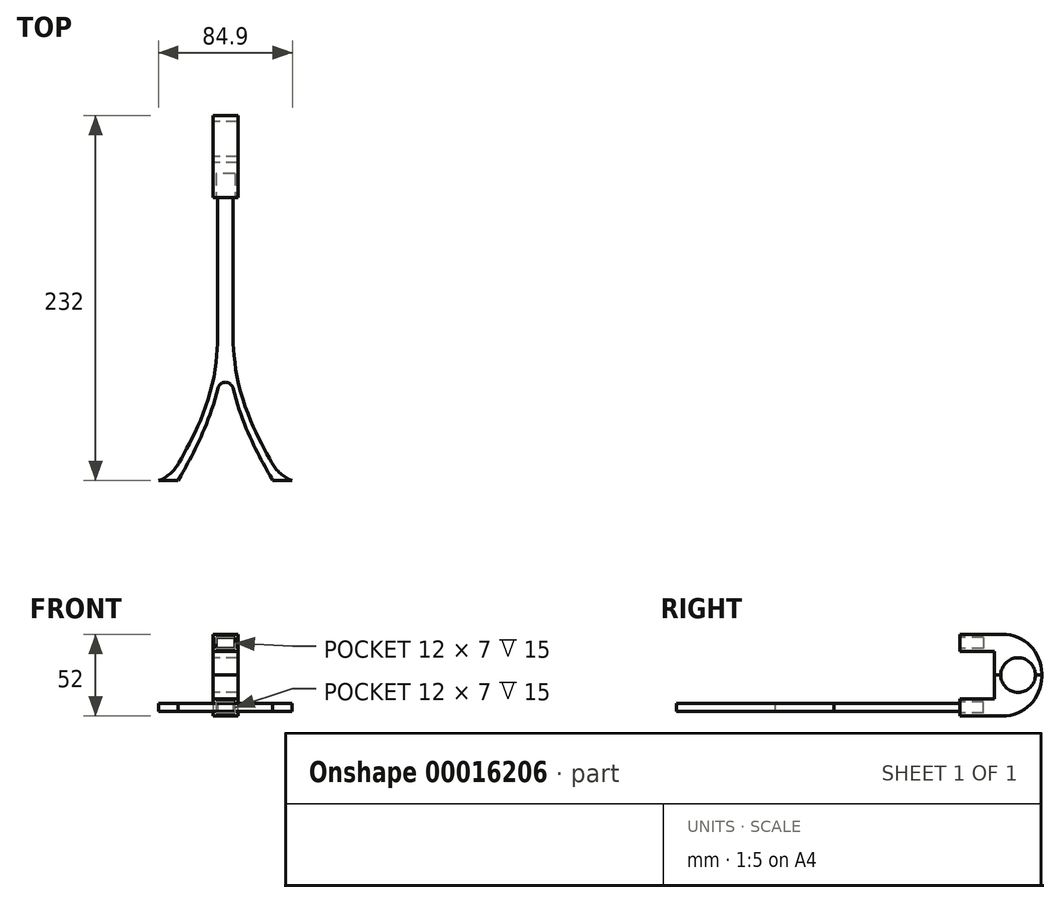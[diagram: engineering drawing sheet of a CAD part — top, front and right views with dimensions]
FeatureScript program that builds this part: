
annotation { "Feature Type Name" : "Feature", "Feature Type Description" : "" }
export const myFeature = defineFeature(function(context is Context, id is Id, definition is map)
    precondition{}
    {
        {
            var Q0;
            Q0=qCreatedBy(makeId("Top.planeOp"),FACE);
            var sketch = newSketch(context, id + "F0", { "sketchPlane" : qUnion([Q0])});
            skLineSegment(sketch, "E0", {"start": v(0, 80) * mm, "end": v(0, 0) * mm});
            skFitSpline(sketch, "E1", {"points": [v(0, 0) * mm, v(30.06, -100) * mm], "startDerivative": vector(-0.28, -149.45) * mm, "endDerivative": vector(29.58, -54.24) * mm});
            skFitSpline(sketch, "E2.0", {"points": [v(5, 0) * mm, v(4.98, -12.12) * mm, v(7.4, -34.14) * mm, v(15.66, -61.06) * mm, v(24.08, -78.77) * mm, v(30.4, -90.34) * mm, v(33.2, -95.3) * mm, v(34.45, -97.6) * mm]});
            skLineSegment(sketch, "E2.1", {"start": v(5, 80) * mm, "end": v(5, 0) * mm});
            skLineSegment(sketch, "E3", {"start": v(0, 80) * mm, "end": v(5, 80) * mm});
            skLineSegment(sketch, "E4", {"start": v(30.06, -100) * mm, "end": v(42.45, -100) * mm});
            skLineSegment(sketch, "E5", {"start": v(42.45, -100) * mm, "end": v(34.24, -97.23) * mm});
            skSolve(sketch);
        }
        {
            var Q0;
            Q0=makeQuery(id+"F0.imprint","IMPRINT",FACE,{"disambiguationData":[TD([[makeQuery(id+"F0.imprint","IMPRINT",EDGE,{"derivedFrom":sQuery(id+"F0.wireOp",EDGE,"E0")}),1.0]])]});
            extrude(context, id + "F1", {"entities" : qUnion([Q0]), "depth" : 5 * mm});
        }
        {
            var Q0;
            Q0=makeQuery(id+"F1.opExtrude","SWEPT_BODY",BODY,{"disambiguationData":[OSD([sQuery(id+"F0.wireOp",EDGE,"E0"),sQuery(id+"F0.wireOp",EDGE,"E1"),sQuery(id+"F0.wireOp",EDGE,"E2.0"),sQuery(id+"F0.wireOp",EDGE,"E2.1"),sQuery(id+"F0.wireOp",EDGE,"E3"),sQuery(id+"F0.wireOp",EDGE,"E4"),sQuery(id+"F0.wireOp",EDGE,"E5")])]});
            var Q1;
            Q1=qCreatedBy(makeId("Right.planeOp"),FACE);
            mirror(context, id + "F2", {"operationType" : NewBodyOperationType.ADD, "entities" : qUnion([Q0]), "mirrorPlane" : qUnion([Q1])});
        }
        {
            var Q0;
            {var subQ0=makeQuery(id+"F1.opExtrude","SWEPT_FACE",FACE,{"disambiguationData":[OSD([sQuery(id+"F0.wireOp",EDGE,"E1")])]});Q0=makeQuery(id+"F2.boolean.opBoolean","INTERSECT",EDGE,{"derivedFrom":[subQ0,makeQuery(id+"F2.opPattern","COPY",FACE,{"derivedFrom":subQ0,"instanceName":"1"})]});}
            fillet(context, id + "F3", {"entities" : qUnion([Q0]), "radius" : 5 * mm, "tangentPropagation" : true, "allowEdgeOverflow" : false});
        }
        {
            var Q0;
            Q0=makeQuery(id+"F2.opPattern","COPY",EDGE,{"derivedFrom":makeQuery(id+"F1.opExtrude","SWEPT_EDGE",EDGE,{"disambiguationData":[OSD([sQuery(id+"F0.wireOp",EDGE,"E2.0"),sQuery(id+"F0.wireOp",EDGE,"E5")])]}),"instanceName":"1"});
            var Q1;
            Q1=makeQuery(id+"F1.opExtrude","SWEPT_EDGE",EDGE,{"disambiguationData":[OSD([sQuery(id+"F0.wireOp",EDGE,"E2.0"),sQuery(id+"F0.wireOp",EDGE,"E5")])]});
            fillet(context, id + "F4", {"entities" : qUnion([Q0, Q1]), "radius" : 25.8 * mm, "tangentPropagation" : true, "allowEdgeOverflow" : false});
        }
        {
            var Q0;
            Q0=makeQuery(id+"F2.opPattern","COPY",EDGE,{"derivedFrom":makeQuery(id+"F1.opExtrude","SWEPT_EDGE",EDGE,{"disambiguationData":[OSD([sQuery(id+"F0.wireOp",EDGE,"E2.1"),sQuery(id+"F0.wireOp",EDGE,"E3")])]}),"instanceName":"1"});
            var Q1;
            Q1=makeQuery(id+"F1.opExtrude","SWEPT_EDGE",EDGE,{"disambiguationData":[OSD([sQuery(id+"F0.wireOp",EDGE,"E2.1"),sQuery(id+"F0.wireOp",EDGE,"E3")])]});
            fillet(context, id + "F5", {"entities" : qUnion([Q0, Q1]), "radius" : 1 * mm, "tangentPropagation" : true, "allowEdgeOverflow" : false});
        }
        {
            var Q0;
            {var subQ0=makeQuery(id+"F1.opExtrude","SWEPT_FACE",FACE,{"disambiguationData":[OSD([sQuery(id+"F0.wireOp",EDGE,"E3")])]});Q0=makeQuery(id+"F2.boolean.opBoolean","MERGE",FACE,{"derivedFrom":[subQ0,makeQuery(id+"F2.opPattern","COPY",FACE,{"derivedFrom":subQ0,"instanceName":"1"})]});}
            var sketch = newSketch(context, id + "F6", { "sketchPlane" : qUnion([Q0])});
            skLineSegment(sketch, "E6.0", {"start": v(4, 6) * mm, "end": v(6, 6) * mm});
            skLineSegment(sketch, "E6.1", {"start": v(4, 6) * mm, "end": v(-4, 6) * mm});
            skLineSegment(sketch, "E6.2", {"start": v(-6, 6) * mm, "end": v(-4, 6) * mm});
            skLineSegment(sketch, "E6.3", {"start": v(-6, -1) * mm, "end": v(-6, 6) * mm});
            skLineSegment(sketch, "E6.4", {"start": v(-4, -1) * mm, "end": v(-6, -1) * mm});
            skLineSegment(sketch, "E6.5", {"start": v(6, 6) * mm, "end": v(6, -1) * mm});
            skLineSegment(sketch, "E6.6", {"start": v(4, -1) * mm, "end": v(-4, -1) * mm});
            skLineSegment(sketch, "E6.7", {"start": v(6, -1) * mm, "end": v(4, -1) * mm});
            skSolve(sketch);
        }
        {
            var Q0;
            Q0 = qSketchRegion(id + "F6", true);
            var Q1;
            Q1 = qConstructionFilter(qBodyType(qCreatedBy(id + "F6" ,EDGE), BodyType.WIRE), ConstructionObject.NO);
            extrude(context, id + "F7", {"entities" : qUnion([Q0]), "surfaceEntities" : qUnion([Q1]), "depth" : 15 * mm});
        }
        {
            var Q0;
            Q0=makeQuery(id+"F7.opExtrude","CAP_FACE",FACE,{"disambiguationData":[OSD([sQuery(id+"F6.wireOp",EDGE,"E6.0"),sQuery(id+"F6.wireOp",EDGE,"E6.1"),sQuery(id+"F6.wireOp",EDGE,"E6.2"),sQuery(id+"F6.wireOp",EDGE,"E6.3"),sQuery(id+"F6.wireOp",EDGE,"E6.4"),sQuery(id+"F6.wireOp",EDGE,"E6.5"),sQuery(id+"F6.wireOp",EDGE,"E6.6"),sQuery(id+"F6.wireOp",EDGE,"E6.7")])],"isStart":true});
            shell(context, id + "F8", {"entities" : qUnion([Q0]), "thickness" : 2 * mm, "oppositeDirection" : true});
        }
        {
            var Q0;
            Q0=makeQuery(id+"F7.opExtrude","CAP_FACE",FACE,{"disambiguationData":[OSD([sQuery(id+"F6.wireOp",EDGE,"E6.0"),sQuery(id+"F6.wireOp",EDGE,"E6.1"),sQuery(id+"F6.wireOp",EDGE,"E6.2"),sQuery(id+"F6.wireOp",EDGE,"E6.3"),sQuery(id+"F6.wireOp",EDGE,"E6.4"),sQuery(id+"F6.wireOp",EDGE,"E6.5"),sQuery(id+"F6.wireOp",EDGE,"E6.6"),sQuery(id+"F6.wireOp",EDGE,"E6.7")])],"isStart":false});
            extrude(context, id + "F9", {"entities" : qUnion([Q0]), "operationType" : NewBodyOperationType.ADD, "depth" : 35 * mm});
        }
        {
            var Q0;
            {var subQ0=sQuery(id+"F6.wireOp",EDGE,"E6.0");var subQ1=sQuery(id+"F6.wireOp",EDGE,"E6.1");var subQ2=sQuery(id+"F6.wireOp",EDGE,"E6.2");Q0=makeQuery(id+"F9.boolean.opBoolean","MERGE",FACE,{"derivedFrom":[makeQuery(id+"F7.opExtrude","SWEPT_FACE",FACE,{"disambiguationData":[OSD([subQ0,subQ1,subQ2])]}),makeQuery(id+"F9.opExtrude","SWEPT_FACE",FACE,{"disambiguationData":[OSD([subQ0,subQ1,subQ2])]})]});}
            var sketch = newSketch(context, id + "F10", { "sketchPlane" : qUnion([Q0])});
            skLineSegment(sketch, "E7.bottom", {"start": v(8, 132) * mm, "end": v(-8, 132) * mm});
            skLineSegment(sketch, "E7.top", {"start": v(8, 102) * mm, "end": v(-8, 102) * mm});
            skLineSegment(sketch, "E7.left", {"start": v(8, 132) * mm, "end": v(8, 102) * mm});
            skLineSegment(sketch, "E7.right", {"start": v(-8, 132) * mm, "end": v(-8, 102) * mm});
            skSolve(sketch);
        }
        {
            var Q0;
            Q0=makeQuery(id+"F10.imprint","IMPRINT",FACE,{"disambiguationData":[TD([[makeQuery(id+"F10.imprint","IMPRINT",EDGE,{"derivedFrom":sQuery(id+"F10.wireOp",EDGE,"E7.bottom")}),1.0]])]});
            extrude(context, id + "F11", {"entities" : qUnion([Q0]), "operationType" : NewBodyOperationType.ADD, "depth" : 15 * mm});
        }
        {
            var Q0;
            Q0=makeQuery(id+"F7.opExtrude","SWEPT_BODY",BODY,{"disambiguationData":[OSD([sQuery(id+"F6.wireOp",EDGE,"E6.0"),sQuery(id+"F6.wireOp",EDGE,"E6.1"),sQuery(id+"F6.wireOp",EDGE,"E6.2"),sQuery(id+"F6.wireOp",EDGE,"E6.3"),sQuery(id+"F6.wireOp",EDGE,"E6.4"),sQuery(id+"F6.wireOp",EDGE,"E6.5"),sQuery(id+"F6.wireOp",EDGE,"E6.6"),sQuery(id+"F6.wireOp",EDGE,"E6.7")])]});
            var Q1;
            Q1=makeQuery(id+"F11.opExtrude","CAP_FACE",FACE,{"disambiguationData":[OSD([sQuery(id+"F10.wireOp",EDGE,"E7.bottom"),sQuery(id+"F10.wireOp",EDGE,"E7.top"),sQuery(id+"F10.wireOp",EDGE,"E7.left"),sQuery(id+"F10.wireOp",EDGE,"E7.right")])],"isStart":false});
            mirror(context, id + "F12", {"operationType" : NewBodyOperationType.ADD, "entities" : qUnion([Q0]), "mirrorPlane" : qUnion([Q1])});
        }
        {
            var Q0;
            {var subQ0=sQuery(id+"F6.wireOp",EDGE,"E6.5");var subQ1=makeQuery(id+"F11.boolean.opBoolean","MERGE",FACE,{"derivedFrom":[makeQuery(id+"F9.boolean.opBoolean","MERGE",FACE,{"derivedFrom":[makeQuery(id+"F7.opExtrude","SWEPT_FACE",FACE,{"disambiguationData":[OSD([subQ0])]}),makeQuery(id+"F9.opExtrude","SWEPT_FACE",FACE,{"disambiguationData":[OSD([subQ0])]})]}),makeQuery(id+"F11.opExtrude","SWEPT_FACE",FACE,{"disambiguationData":[OSD([sQuery(id+"F10.wireOp",EDGE,"E7.right")])]})]});Q0=makeQuery(id+"F12.boolean.opBoolean","MERGE",FACE,{"derivedFrom":[subQ1,makeQuery(id+"F12.opPattern","COPY",FACE,{"derivedFrom":subQ1,"instanceName":"1"})]});}
            var sketch = newSketch(context, id + "F13", { "sketchPlane" : qUnion([Q0])});
            skLineSegment(sketch, "E8", {"start": v(-102, 23) * mm, "end": v(-132, 23) * mm, "construction": true});
            skCircle(sketch, "E9", {"center": v(-117, 23) * mm, "radius": 11 * mm});
            skSolve(sketch);
        }
        {
            var Q0;
            Q0 = qSketchRegion(id + "F13", true);
            var Q1;
            Q1 = qConstructionFilter(qBodyType(qCreatedBy(id + "F13" ,EDGE), BodyType.WIRE), ConstructionObject.NO);
            extrude(context, id + "F14", {"entities" : qUnion([Q0]), "operationType" : NewBodyOperationType.REMOVE, "surfaceEntities" : qUnion([Q1]), "endBound" : BoundingType.THROUGH_ALL, "oppositeDirection" : true, "depth" : 25 * mm});
        }
        {
            var Q0;
            Q0=makeQuery(id+"F9.opExtrude","CAP_EDGE",EDGE,{"disambiguationData":[OSD([sQuery(id+"F6.wireOp",EDGE,"E6.4"),sQuery(id+"F6.wireOp",EDGE,"E6.6"),sQuery(id+"F6.wireOp",EDGE,"E6.7")])],"isStart":false});
            var Q1;
            Q1=makeQuery(id+"F12.opPattern","COPY",EDGE,{"derivedFrom":makeQuery(id+"F9.opExtrude","CAP_EDGE",EDGE,{"disambiguationData":[OSD([sQuery(id+"F6.wireOp",EDGE,"E6.4"),sQuery(id+"F6.wireOp",EDGE,"E6.6"),sQuery(id+"F6.wireOp",EDGE,"E6.7")])],"isStart":false}),"instanceName":"1"});
            fillet(context, id + "F15", {"entities" : qUnion([Q0, Q1]), "radius" : 25 * mm, "tangentPropagation" : true, "allowEdgeOverflow" : false});
        }
    });
